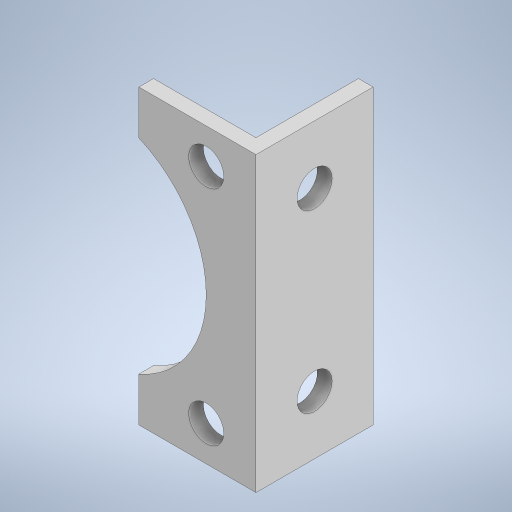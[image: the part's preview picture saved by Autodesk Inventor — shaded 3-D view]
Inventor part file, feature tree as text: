
AUTODESK INVENTOR PART (.ipt)
format: ipt  version: 2023 (Build 270158000, 158)  size: 247,296 bytes
history: native  units: in
note: dims shown in document units (in); Inventor stores cm internally (conversion verified against a paired STEP export)
features: extrude x3, sketch x3
ambient origin geometry x8: Origin, YZ Plane, XZ Plane, XY Plane, X Axis, Y Axis, Z Axis, Center Point
bodies: Solid1 (feature_tree)
feature tree (6):
  extrude  "Extrusion1"  Depth=0.125in
  extrude  "Extrusion2"  Depth=0.875in
  extrude  "Extrusion3"  Depth=2.5in
  sketch  "Sketch1"  dims[d0=1.0in d1=0.125in]
  sketch  "Sketch2"  dims[d2=0.875in d3=0.875in]
  sketch  "Sketch3"  dims[d4=2.5in d5=0.0in d6=0.25in d9=0.3in d10=0.3in d13=2.5in d14=0.0in d18=2.5in d19=0.0in]
